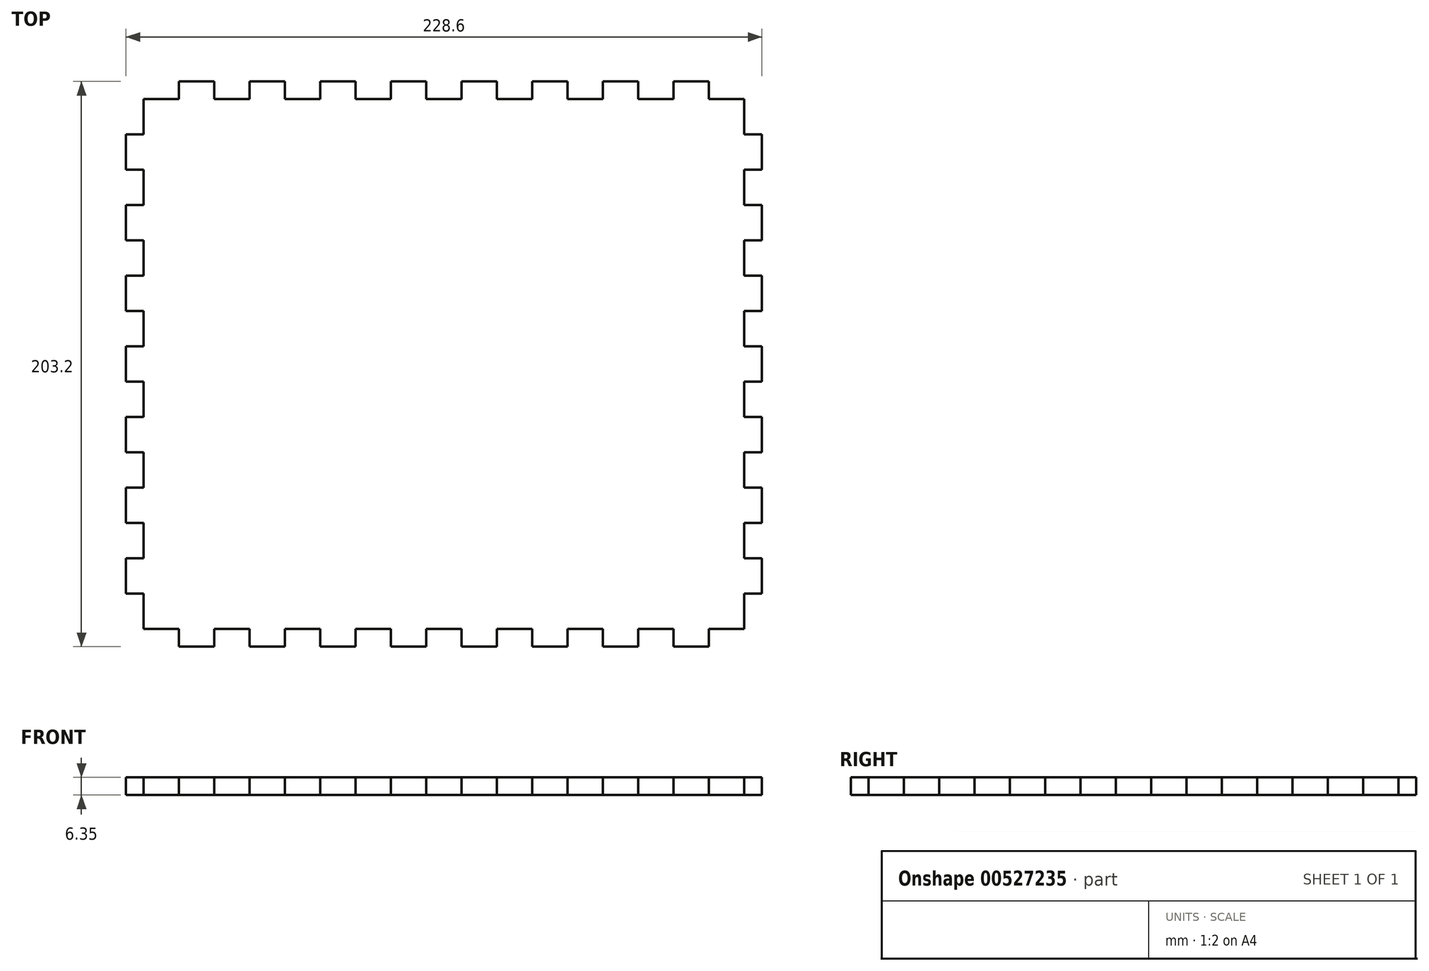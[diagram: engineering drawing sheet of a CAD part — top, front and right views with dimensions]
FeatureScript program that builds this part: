
annotation { "Feature Type Name" : "Feature", "Feature Type Description" : "" }
export const myFeature = defineFeature(function(context is Context, id is Id, definition is map)
    precondition{}
    {
        {
            var Q0;
            Q0=qCreatedBy(makeId("Top.planeOp"),FACE);
            var sketch = newSketch(context, id + "F0", { "sketchPlane" : qUnion([Q0])});
            skLineSegment(sketch, "E0", {"start": v(6.35, -6.35) * mm, "end": v(19.05, -6.35) * mm});
            skLineSegment(sketch, "E1", {"start": v(19.05, -6.35) * mm, "end": v(19.05, 0) * mm});
            skLineSegment(sketch, "E2", {"start": v(19.05, 0) * mm, "end": v(31.75, 0) * mm});
            skLineSegment(sketch, "E3", {"start": v(31.75, 0) * mm, "end": v(31.75, -6.35) * mm});
            skLineSegment(sketch, "E4", {"start": v(31.75, -6.35) * mm, "end": v(44.45, -6.35) * mm});
            skLineSegment(sketch, "E5", {"start": v(44.45, -6.35) * mm, "end": v(44.45, 0) * mm});
            skLineSegment(sketch, "E6", {"start": v(44.45, 0) * mm, "end": v(57.15, 0) * mm});
            skLineSegment(sketch, "E7", {"start": v(57.15, 0) * mm, "end": v(57.15, -6.35) * mm});
            skLineSegment(sketch, "E8", {"start": v(57.15, -6.35) * mm, "end": v(69.85, -6.35) * mm});
            skLineSegment(sketch, "E9", {"start": v(69.85, -6.35) * mm, "end": v(69.85, 0) * mm});
            skLineSegment(sketch, "E10", {"start": v(69.85, 0) * mm, "end": v(82.55, 0) * mm});
            skLineSegment(sketch, "E11", {"start": v(82.55, 0) * mm, "end": v(82.55, -6.35) * mm});
            skLineSegment(sketch, "E12", {"start": v(82.55, -6.35) * mm, "end": v(95.25, -6.35) * mm});
            skLineSegment(sketch, "E13", {"start": v(95.25, -6.35) * mm, "end": v(95.25, 0) * mm});
            skLineSegment(sketch, "E14.trimOffspring", {"start": v(95.25, 0) * mm, "end": v(107.95, 0) * mm});
            skLineSegment(sketch, "E15", {"start": v(107.95, 0) * mm, "end": v(107.95, -6.35) * mm});
            skLineSegment(sketch, "E16", {"start": v(107.95, -6.35) * mm, "end": v(120.65, -6.35) * mm});
            skLineSegment(sketch, "E17", {"start": v(120.65, -6.35) * mm, "end": v(120.65, 0) * mm});
            skLineSegment(sketch, "E18", {"start": v(120.65, 0) * mm, "end": v(133.35, 0) * mm});
            skLineSegment(sketch, "E19", {"start": v(133.35, 0) * mm, "end": v(133.35, -6.35) * mm});
            skLineSegment(sketch, "E20", {"start": v(133.35, -6.35) * mm, "end": v(146.05, -6.35) * mm});
            skLineSegment(sketch, "E21", {"start": v(146.05, -6.35) * mm, "end": v(146.05, 0) * mm});
            skLineSegment(sketch, "E22", {"start": v(146.05, 0) * mm, "end": v(158.75, 0) * mm});
            skLineSegment(sketch, "E23", {"start": v(158.75, 0) * mm, "end": v(158.75, -6.35) * mm});
            skLineSegment(sketch, "E24", {"start": v(158.75, -6.35) * mm, "end": v(171.45, -6.35) * mm});
            skLineSegment(sketch, "E25", {"start": v(171.45, -6.35) * mm, "end": v(171.45, 0) * mm});
            skLineSegment(sketch, "E26.trimOffspring", {"start": v(171.45, 0) * mm, "end": v(184.15, 0) * mm});
            skLineSegment(sketch, "E27", {"start": v(184.15, 0) * mm, "end": v(184.15, -6.35) * mm});
            skLineSegment(sketch, "E28", {"start": v(184.15, -6.35) * mm, "end": v(196.85, -6.35) * mm});
            skLineSegment(sketch, "E29", {"start": v(196.85, -6.35) * mm, "end": v(196.85, 0) * mm});
            skLineSegment(sketch, "E30", {"start": v(196.85, 0) * mm, "end": v(209.55, 0) * mm});
            skLineSegment(sketch, "E31", {"start": v(209.55, 0) * mm, "end": v(209.55, -6.35) * mm});
            skLineSegment(sketch, "E32", {"start": v(209.55, -6.35) * mm, "end": v(222.25, -6.35) * mm});
            skPoint(sketch, "E33.orphan", {"position": v(228.6, 0) * mm});
            skLineSegment(sketch, "E34", {"start": v(6.35, -6.35) * mm, "end": v(6.35, -19.05) * mm});
            skLineSegment(sketch, "E35", {"start": v(6.35, -19.05) * mm, "end": v(0, -19.05) * mm});
            skLineSegment(sketch, "E36.trimOffspring", {"start": v(0, -19.05) * mm, "end": v(0, -31.75) * mm});
            skPoint(sketch, "E37.left.start.orphan", {"position": v(0, 0) * mm});
            skLineSegment(sketch, "E38", {"start": v(0, -31.75) * mm, "end": v(6.35, -31.75) * mm});
            skLineSegment(sketch, "E39", {"start": v(6.35, -31.75) * mm, "end": v(6.35, -44.45) * mm});
            skLineSegment(sketch, "E40", {"start": v(6.35, -44.45) * mm, "end": v(0, -44.45) * mm});
            skLineSegment(sketch, "E41", {"start": v(0, -44.45) * mm, "end": v(0, -57.15) * mm});
            skLineSegment(sketch, "E42", {"start": v(0, -57.15) * mm, "end": v(6.35, -57.15) * mm});
            skLineSegment(sketch, "E43", {"start": v(6.35, -57.15) * mm, "end": v(6.35, -69.85) * mm});
            skLineSegment(sketch, "E44", {"start": v(6.35, -69.85) * mm, "end": v(0, -69.85) * mm});
            skLineSegment(sketch, "E45.trimOffspring", {"start": v(0, -69.85) * mm, "end": v(0, -82.55) * mm});
            skLineSegment(sketch, "E46", {"start": v(0, -82.55) * mm, "end": v(6.35, -82.55) * mm});
            skLineSegment(sketch, "E47", {"start": v(6.35, -82.55) * mm, "end": v(6.35, -95.25) * mm});
            skLineSegment(sketch, "E48", {"start": v(6.35, -95.25) * mm, "end": v(0, -95.25) * mm});
            skLineSegment(sketch, "E49", {"start": v(0, -95.25) * mm, "end": v(0, -107.95) * mm});
            skLineSegment(sketch, "E50", {"start": v(0, -107.95) * mm, "end": v(6.35, -107.95) * mm});
            skLineSegment(sketch, "E51", {"start": v(6.35, -107.95) * mm, "end": v(6.35, -120.65) * mm});
            skLineSegment(sketch, "E52", {"start": v(6.35, -120.65) * mm, "end": v(0, -120.65) * mm});
            skLineSegment(sketch, "E53", {"start": v(0, -120.65) * mm, "end": v(0, -133.35) * mm});
            skLineSegment(sketch, "E54", {"start": v(0, -133.35) * mm, "end": v(6.35, -133.35) * mm});
            skLineSegment(sketch, "E55", {"start": v(6.35, -133.35) * mm, "end": v(6.35, -146.05) * mm});
            skLineSegment(sketch, "E56", {"start": v(6.35, -146.05) * mm, "end": v(0, -146.05) * mm});
            skLineSegment(sketch, "E57.trimOffspring", {"start": v(0, -146.05) * mm, "end": v(0, -158.75) * mm});
            skLineSegment(sketch, "E58", {"start": v(0, -158.75) * mm, "end": v(6.35, -158.75) * mm});
            skLineSegment(sketch, "E59", {"start": v(6.35, -158.75) * mm, "end": v(6.35, -171.45) * mm});
            skLineSegment(sketch, "E60", {"start": v(6.35, -171.45) * mm, "end": v(0, -171.45) * mm});
            skLineSegment(sketch, "E61.trimOffspring", {"start": v(0, -171.45) * mm, "end": v(0, -184.15) * mm});
            skLineSegment(sketch, "E62", {"start": v(0, -184.15) * mm, "end": v(6.35, -184.15) * mm});
            skLineSegment(sketch, "E63", {"start": v(6.35, -184.15) * mm, "end": v(6.35, -196.85) * mm});
            skLineSegment(sketch, "E64", {"start": v(6.35, -196.85) * mm, "end": v(19.05, -196.85) * mm});
            skLineSegment(sketch, "E65", {"start": v(19.05, -196.85) * mm, "end": v(19.05, -203.2) * mm});
            skPoint(sketch, "E66.orphan", {"position": v(0, -203.2) * mm});
            skLineSegment(sketch, "E67", {"start": v(114.3, -6.35) * mm, "end": v(114.3, -48.8) * mm, "construction": true});
            skLineSegment(sketch, "E68", {"start": v(0, -101.6) * mm, "end": v(54.1, -101.6) * mm, "construction": true});
            skLineSegment(sketch, "E69.MirrorCS", {"start": v(228.6, -101.6) * mm, "end": v(174.5, -101.6) * mm, "construction": true});
            skLineSegment(sketch, "E70.MirrorCS", {"start": v(222.25, -6.35) * mm, "end": v(222.25, -19.05) * mm});
            skLineSegment(sketch, "E71.MirrorCS", {"start": v(222.25, -19.05) * mm, "end": v(228.6, -19.05) * mm});
            skLineSegment(sketch, "E72.MirrorCS", {"start": v(228.6, -19.05) * mm, "end": v(228.6, -31.75) * mm});
            skLineSegment(sketch, "E73.MirrorCS", {"start": v(228.6, -31.75) * mm, "end": v(222.25, -31.75) * mm});
            skLineSegment(sketch, "E74.MirrorCS", {"start": v(222.25, -31.75) * mm, "end": v(222.25, -44.45) * mm});
            skLineSegment(sketch, "E75.MirrorCS", {"start": v(222.25, -44.45) * mm, "end": v(228.6, -44.45) * mm});
            skLineSegment(sketch, "E76.MirrorCS", {"start": v(228.6, -44.45) * mm, "end": v(228.6, -57.15) * mm});
            skLineSegment(sketch, "E77.MirrorCS", {"start": v(228.6, -57.15) * mm, "end": v(222.25, -57.15) * mm});
            skLineSegment(sketch, "E78.MirrorCS", {"start": v(222.25, -57.15) * mm, "end": v(222.25, -69.85) * mm});
            skLineSegment(sketch, "E79.MirrorCS", {"start": v(222.25, -69.85) * mm, "end": v(228.6, -69.85) * mm});
            skLineSegment(sketch, "E80.MirrorCS", {"start": v(228.6, -69.85) * mm, "end": v(228.6, -82.55) * mm});
            skLineSegment(sketch, "E81.MirrorCS", {"start": v(228.6, -82.55) * mm, "end": v(222.25, -82.55) * mm});
            skLineSegment(sketch, "E82.MirrorCS", {"start": v(222.25, -82.55) * mm, "end": v(222.25, -95.25) * mm});
            skLineSegment(sketch, "E83.MirrorCS", {"start": v(222.25, -95.25) * mm, "end": v(228.6, -95.25) * mm});
            skLineSegment(sketch, "E84.MirrorCS", {"start": v(228.6, -95.25) * mm, "end": v(228.6, -107.95) * mm});
            skLineSegment(sketch, "E85.MirrorCS", {"start": v(228.6, -107.95) * mm, "end": v(222.25, -107.95) * mm});
            skLineSegment(sketch, "E86.MirrorCS", {"start": v(222.25, -107.95) * mm, "end": v(222.25, -120.65) * mm});
            skLineSegment(sketch, "E87.MirrorCS", {"start": v(222.25, -120.65) * mm, "end": v(228.6, -120.65) * mm});
            skLineSegment(sketch, "E88.MirrorCS", {"start": v(228.6, -120.65) * mm, "end": v(228.6, -133.35) * mm});
            skLineSegment(sketch, "E89.MirrorCS", {"start": v(228.6, -133.35) * mm, "end": v(222.25, -133.35) * mm});
            skLineSegment(sketch, "E90.MirrorCS", {"start": v(222.25, -133.35) * mm, "end": v(222.25, -146.05) * mm});
            skLineSegment(sketch, "E91.MirrorCS", {"start": v(222.25, -146.05) * mm, "end": v(228.6, -146.05) * mm});
            skLineSegment(sketch, "E92.MirrorCS", {"start": v(228.6, -146.05) * mm, "end": v(228.6, -158.75) * mm});
            skLineSegment(sketch, "E93.MirrorCS", {"start": v(228.6, -158.75) * mm, "end": v(222.25, -158.75) * mm});
            skLineSegment(sketch, "E94.MirrorCS", {"start": v(222.25, -158.75) * mm, "end": v(222.25, -171.45) * mm});
            skLineSegment(sketch, "E95.MirrorCS", {"start": v(222.25, -171.45) * mm, "end": v(228.6, -171.45) * mm});
            skLineSegment(sketch, "E96.MirrorCS", {"start": v(228.6, -171.45) * mm, "end": v(228.6, -184.15) * mm});
            skLineSegment(sketch, "E97.MirrorCS", {"start": v(228.6, -184.15) * mm, "end": v(222.25, -184.15) * mm});
            skLineSegment(sketch, "E98.MirrorCS", {"start": v(222.25, -184.15) * mm, "end": v(222.25, -196.85) * mm});
            skLineSegment(sketch, "E99.MirrorCS", {"start": v(222.25, -196.85) * mm, "end": v(209.55, -196.85) * mm});
            skLineSegment(sketch, "E100.MirrorCS", {"start": v(209.55, -196.85) * mm, "end": v(209.55, -203.2) * mm});
            skLineSegment(sketch, "E101.MirrorCS", {"start": v(19.05, -203.2) * mm, "end": v(31.75, -203.2) * mm});
            skLineSegment(sketch, "E102.MirrorCS", {"start": v(31.75, -203.2) * mm, "end": v(31.75, -196.85) * mm});
            skLineSegment(sketch, "E103.MirrorCS", {"start": v(31.75, -196.85) * mm, "end": v(44.45, -196.85) * mm});
            skLineSegment(sketch, "E104.MirrorCS", {"start": v(44.45, -196.85) * mm, "end": v(44.45, -203.2) * mm});
            skLineSegment(sketch, "E105.MirrorCS", {"start": v(44.45, -203.2) * mm, "end": v(57.15, -203.2) * mm});
            skLineSegment(sketch, "E106.MirrorCS", {"start": v(57.15, -203.2) * mm, "end": v(57.15, -196.85) * mm});
            skLineSegment(sketch, "E107.MirrorCS", {"start": v(57.15, -196.85) * mm, "end": v(69.85, -196.85) * mm});
            skLineSegment(sketch, "E108.MirrorCS", {"start": v(69.85, -196.85) * mm, "end": v(69.85, -203.2) * mm});
            skLineSegment(sketch, "E109.MirrorCS", {"start": v(69.85, -203.2) * mm, "end": v(82.55, -203.2) * mm});
            skLineSegment(sketch, "E110.MirrorCS", {"start": v(82.55, -203.2) * mm, "end": v(82.55, -196.85) * mm});
            skLineSegment(sketch, "E111.MirrorCS", {"start": v(82.55, -196.85) * mm, "end": v(95.25, -196.85) * mm});
            skLineSegment(sketch, "E112.MirrorCS", {"start": v(95.25, -196.85) * mm, "end": v(95.25, -203.2) * mm});
            skLineSegment(sketch, "E113.MirrorCS", {"start": v(95.25, -203.2) * mm, "end": v(107.95, -203.2) * mm});
            skLineSegment(sketch, "E114.MirrorCS", {"start": v(107.95, -203.2) * mm, "end": v(107.95, -196.85) * mm});
            skLineSegment(sketch, "E115.MirrorCS", {"start": v(107.95, -196.85) * mm, "end": v(120.65, -196.85) * mm});
            skLineSegment(sketch, "E116.MirrorCS", {"start": v(120.65, -196.85) * mm, "end": v(120.65, -203.2) * mm});
            skLineSegment(sketch, "E117.MirrorCS", {"start": v(120.65, -203.2) * mm, "end": v(133.35, -203.2) * mm});
            skLineSegment(sketch, "E118.MirrorCS", {"start": v(133.35, -203.2) * mm, "end": v(133.35, -196.85) * mm});
            skLineSegment(sketch, "E119.MirrorCS", {"start": v(133.35, -196.85) * mm, "end": v(146.05, -196.85) * mm});
            skLineSegment(sketch, "E120.MirrorCS", {"start": v(146.05, -196.85) * mm, "end": v(146.05, -203.2) * mm});
            skLineSegment(sketch, "E121.MirrorCS", {"start": v(146.05, -203.2) * mm, "end": v(158.75, -203.2) * mm});
            skLineSegment(sketch, "E122.MirrorCS", {"start": v(158.75, -203.2) * mm, "end": v(158.75, -196.85) * mm});
            skLineSegment(sketch, "E123.MirrorCS", {"start": v(158.75, -196.85) * mm, "end": v(171.45, -196.85) * mm});
            skLineSegment(sketch, "E124.MirrorCS", {"start": v(171.45, -196.85) * mm, "end": v(171.45, -203.2) * mm});
            skLineSegment(sketch, "E125.MirrorCS", {"start": v(171.45, -203.2) * mm, "end": v(184.15, -203.2) * mm});
            skLineSegment(sketch, "E126.MirrorCS", {"start": v(184.15, -203.2) * mm, "end": v(184.15, -196.85) * mm});
            skLineSegment(sketch, "E127.MirrorCS", {"start": v(184.15, -196.85) * mm, "end": v(196.85, -196.85) * mm});
            skLineSegment(sketch, "E128.MirrorCS", {"start": v(196.85, -196.85) * mm, "end": v(196.85, -203.2) * mm});
            skLineSegment(sketch, "E129.MirrorCS", {"start": v(196.85, -203.2) * mm, "end": v(209.55, -203.2) * mm});
            skSolve(sketch);
        }
        {
            var Q0;
            Q0=makeQuery(id+"F0.imprint","IMPRINT",FACE,{"disambiguationData":[TD([[makeQuery(id+"F0.imprint","IMPRINT",EDGE,{"derivedFrom":sQuery(id+"F0.wireOp",EDGE,"E0")}),-1.0]])]});
            extrude(context, id + "F1", {"entities" : qUnion([Q0]), "depth" : 6.35 * mm, "offsetDistance" : 25.4 * mm});
        }
    });
